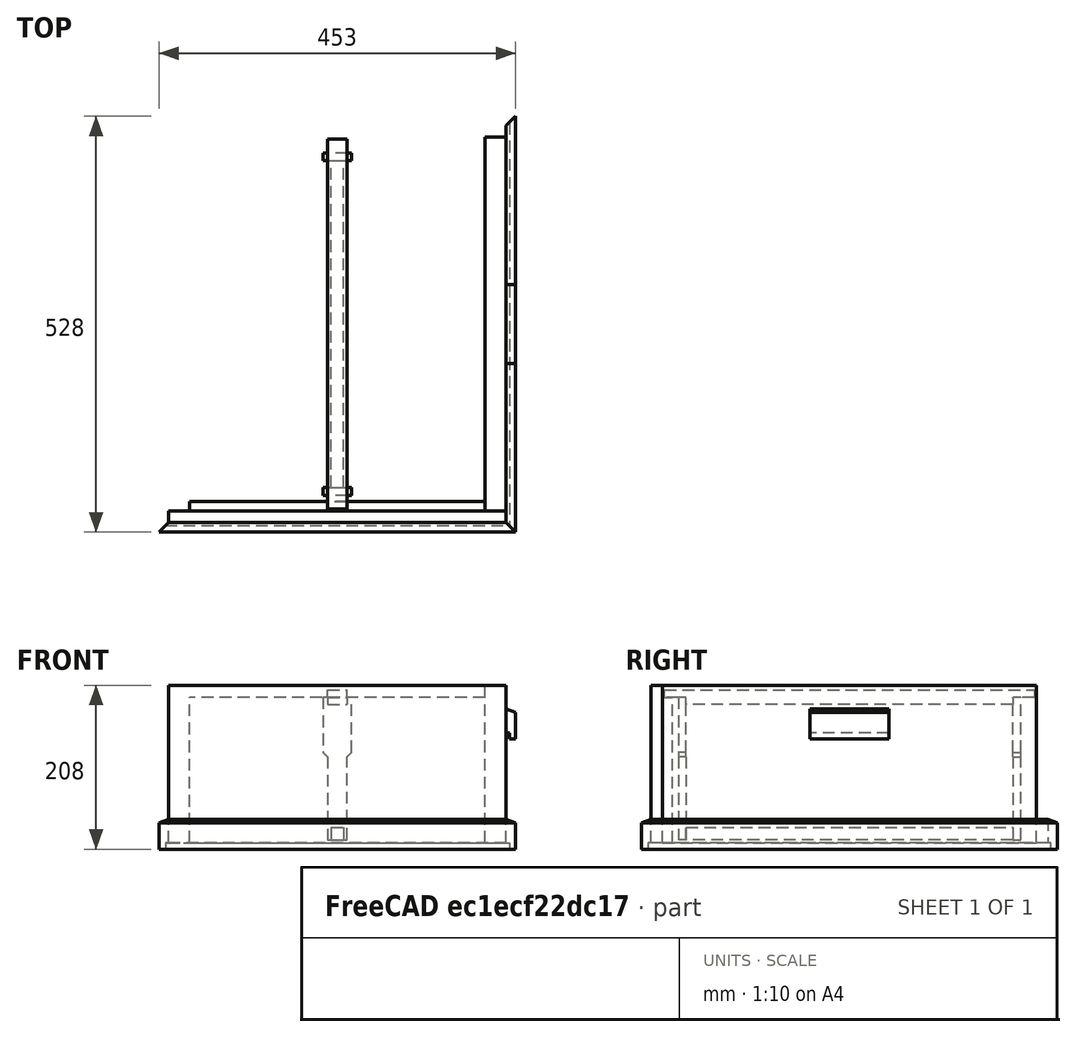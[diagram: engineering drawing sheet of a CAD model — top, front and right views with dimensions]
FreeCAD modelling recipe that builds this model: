
FCSTD DOCUMENT  (FreeCAD 0.19R)
Label: naklada_nizka
License: All rights reserved
LicenseURL: http://en.wikipedia.org/wiki/All_rights_reserved
objects: TechDraw::DrawViewDimension×33, App::Link×20, PartDesign::CoordinateSystem×16, Sketcher::SketchObject×12, TechDraw::DrawProjGroupItem×10, PartDesign::Pad×9, App::Part×7, PartDesign::Body×6, TechDraw::DrawProjGroup×5, TechDraw::DrawViewPart×4, TechDraw::DrawRichAnno×4, App::DocumentObjectGroup×3, PartDesign::Pocket×3, TechDraw::DrawSVGTemplate×3, TechDraw::DrawPage×3, TechDraw::DrawViewSection×2, TechDraw::DrawViewAnnotation×2, App::FeaturePython×1
note: 58 computed .brp shape members not serialized (recipe doc carries the construction recipe); baked Part::Feature solids carry a one-line shape summary decoded from their .brp

FEATURE [PartDesign::CoordinateSystem] LCS_Origin
  AttacherType = Attacher::AttachEngine3D
  MapMode = 2
  Support = -> [X_Axis]
FEATURE [App::FeaturePython] Variables  # WARN: FeaturePython — macro-defined, semantics opaque (R4)
  Type = App::PropertyContainer
  frame_cut = 15
  frame_height = 190
  frame_spacing = 37.5
  height = 200
  inner_depth = 450
  inner_width = 375
  wall_cut = 12.5
  wall_thickness = 27
FEATURE [App::DocumentObjectGroup] Constraints
FEATURE [App::DocumentObjectGroup] Configurations
FEATURE [PartDesign::CoordinateSystem] LCS_0
  AttacherType = Attacher::AttachEngine3D
  MapMode = 2
  Support = -> [X_Axis001]
FEATURE [PartDesign::CoordinateSystem] LCS_0001
  AttacherType = Attacher::AttachEngine3D
  MapMode = 2
  Support = -> [X_Axis002]
FEATURE [Sketcher::SketchObject] Sketch  label="Sketch001"
  FullyConstrained = true
  MapMode = 5
  Support = -> [XY_Plane002]
  expr: Constraints[16] = Variables.inner_width
  expr: Constraints[17] = Variables.wall_thickness
  expr: Constraints[22] = Variables.inner_depth / 2
  expr: Constraints[19] = Variables.wall_thickness
  expr: Constraints[18] = Variables.wall_cut
  sketch-geometry (8):
    g0: LineSegment StartX=-187.5 StartY=-225 StartZ=0 EndX=187.5 EndY=-225 EndZ=0
    g1: LineSegment StartX=187.5 StartY=-225 StartZ=0 EndX=187.5 EndY=-237.5 EndZ=0
    g2: LineSegment StartX=187.5 StartY=-237.5 StartZ=0 EndX=214.5 EndY=-237.5 EndZ=0
    g3: LineSegment StartX=214.5 StartY=-237.5 StartZ=0 EndX=214.5 EndY=-252 EndZ=0
    g4: LineSegment StartX=214.5 StartY=-252 StartZ=0 EndX=-214.5 EndY=-252 EndZ=0
    g5: LineSegment StartX=-214.5 StartY=-252 StartZ=0 EndX=-214.5 EndY=-237.5 EndZ=0
    g6: LineSegment StartX=-214.5 StartY=-237.5 StartZ=0 EndX=-187.5 EndY=-237.5 EndZ=0
    g7: LineSegment StartX=-187.5 StartY=-237.5 StartZ=0 EndX=-187.5 EndY=-225 EndZ=0
  constraints (23):
    c: Coincident(g0,g1)
    c: Coincident(g1,g2)
    c: Horizontal(g2)
    c: Coincident(g2,g3)
    c: Vertical(g3)
    c: Coincident(g3,g4)
    c: Horizontal(g4)
    c: Coincident(g4,g5)
    c: Vertical(g5)
    c: Coincident(g5,g6)
    c: Horizontal(g6)
    c: Coincident(g6,g7)
    c: Vertical(g7)
    c: Vertical(g1)
    c: Horizontal(g6,g1)
    c: Equal(g6,g2)
    c: DistanceX(g0,g0) = 375
    c: DistanceX(g2,g2) = 27
    c: DistanceY(g1,g1) = 12.5
    c: DistanceY(g3,g0) = 27
    c: Coincident(g0,g7)
    c: Symmetric(g0,g0,g-2)
    c: DistanceY(g0,g-1) = 225
FEATURE [PartDesign::Pad] Pad
  Direction = (1,1,1)
  Length = 200
  Length2 = 100
  Profile = -> Sketch
  Type = 0
  expr: Length = Variables.height
FEATURE [Sketcher::SketchObject] Sketch001  label="Sketch002"
  ExternalGeometry = -> [Pad]
  FullyConstrained = true
  MapMode = 5
  Placement = pos=(0,0,0) rot=(0.57735,0.57735,0.57735;2.0944rad)
  Support = -> [YZ_Plane002]
  expr: Constraints[9] = Variables.frame_cut
  sketch-geometry (4):
    g0: LineSegment StartX=-225 StartY=200 StartZ=0 EndX=-237.5 EndY=200 EndZ=0
    g1: LineSegment StartX=-237.5 StartY=200 StartZ=0 EndX=-237.5 EndY=185 EndZ=0
    g2: LineSegment StartX=-237.5 StartY=185 StartZ=0 EndX=-225 EndY=185 EndZ=0
    g3: LineSegment StartX=-225 StartY=185 StartZ=0 EndX=-225 EndY=200 EndZ=0
  constraints (10):
    c: Coincident(g0,g1)
    c: Coincident(g1,g2)
    c: Coincident(g2,g3)
    c: Coincident(g3,g0)
    c: Horizontal(g2)
    c: Vertical(g1)
    c: Vertical(g3)
    c: Coincident(g0,g-3)
    c: Coincident(g0,g-3)
    c: DistanceY(g3,g3) = 15
FEATURE [PartDesign::Pocket] Pocket
  BaseFeature = -> Pad
  Length = 5
  Length2 = 100
  Midplane = true
  Profile = -> Sketch001
  Type = 1
FEATURE [PartDesign::Body] Body
  Group = -> [LCS_0001,Sketch,Pad,Sketch001,Pocket]
  Origin = -> Origin002
  Tip = -> Pocket
FEATURE [App::Part] Wall_rear  label="wall_front_rear"
  Group = -> [LCS_0,Body]
  LabelDocUser = naklada
  LabelPartUser = Wall_rear
  Origin = -> Origin001
  PadLengthUser = 305.0 
  ShapeLengthUser = 890
  ShapeVolumeUser = 305.0 mm x 25.0 mm x 420.0 mm
FEATURE [App::Link] Wall_rear001  label="wall_front"
  AssemblyType = Part::Link
  AttachedBy = #LCS_0
  AttachedTo = Parent Assembly#LCS_Origin
  LinkedObject = -> Wall_rear
  SolverId = Asm4EE
  expr: Placement = LCS_Origin.Placement * AttachmentOffset * LCS_0.Placement ^ -1
FEATURE [App::Link] Wall_rear002  label="wall_rear"
  AssemblyType = Part::Link
  AttachedBy = #LCS_0
  AttachedTo = Parent Assembly#LCS_Origin
  AttachmentOffset = pos=(0,0,0) rot=(0,0,1;3.14159rad)
  LinkPlacement = pos=(0,0,0) rot=(0,0,1;3.14159rad)
  LinkedObject = -> Wall_rear
  Placement = pos=(0,0,0) rot=(0,0,1;3.14159rad)
  SolverId = Asm4EE
  expr: Placement = LCS_Origin.Placement * AttachmentOffset * LCS_0.Placement ^ -1
FEATURE [PartDesign::CoordinateSystem] LCS_0002  label="LCS_21"
  AttacherType = Attacher::AttachEngine3D
  MapMode = 2
  Support = -> [X_Axis003]
FEATURE [PartDesign::CoordinateSystem] LCS_0003
  AttacherType = Attacher::AttachEngine3D
  MapMode = 2
  Support = -> [X_Axis004]
FEATURE [Sketcher::SketchObject] Sketch002  label="Sketch003"
  FullyConstrained = true
  MapMode = 5
  Support = -> [XY_Plane004]
  expr: Constraints[6] = Variables.wall_thickness
  expr: Constraints[7] = Variables.inner_depth + Variables.wall_cut * 2
  expr: Constraints[8] = Variables.inner_width / 2
  sketch-geometry (4):
    g0: LineSegment StartX=187.5 StartY=-237.5 StartZ=0 EndX=214.5 EndY=-237.5 EndZ=0
    g1: LineSegment StartX=214.5 StartY=-237.5 StartZ=0 EndX=214.5 EndY=237.5 EndZ=0
    g2: LineSegment StartX=214.5 StartY=237.5 StartZ=0 EndX=187.5 EndY=237.5 EndZ=0
    g3: LineSegment StartX=187.5 StartY=237.5 StartZ=0 EndX=187.5 EndY=-237.5 EndZ=0
  constraints (11):
    c: Coincident(g0,g1)
    c: Coincident(g1,g2)
    c: Coincident(g2,g3)
    c: Coincident(g3,g0)
    c: Horizontal(g0)
    c: Horizontal(g2)
    c: DistanceX(g0,g0) = 27
    c: DistanceY(g1,g1) = 475
    c: DistanceX(g-1,g0) = 187.5
    c: Vertical(g1)
    c: Symmetric(g0,g2,g-1)
FEATURE [PartDesign::Pad] Pad001
  Direction = (1,1,1)
  Length = 200
  Length2 = 100
  Profile = -> Sketch002
  Type = 0
  expr: Length = Variables.height
FEATURE [PartDesign::Body] Body_2
  Group = -> [LCS_0003,Sketch002,Pad001]
  Origin = -> Origin004
  Tip = -> Pad001
FEATURE [App::Part] wall_side
  Group = -> [LCS_0002,Body_2]
  LabelDocUser = naklada
  LabelPartUser = wall_side
  Origin = -> Origin003
  PadLengthUser = 305.0 
  ShapeLengthUser = 1000
  ShapeVolumeUser = 305.0 mm x 475.0 mm x 25.0 mm
FEATURE [App::Link] wall_side001  label="wall_right"
  AssemblyType = Part::Link
  AttachedBy = #LCS_0002
  AttachedTo = Parent Assembly#LCS_Origin
  LinkedObject = -> wall_side
  SolverId = Asm4EE
  expr: Placement = LCS_Origin.Placement * AttachmentOffset * LCS_0002.Placement ^ -1
FEATURE [App::Link] wall  label="wall_left"
  AssemblyType = Part::Link
  AttachedBy = #LCS_0002
  AttachedTo = Parent Assembly#LCS_Origin
  AttachmentOffset = pos=(0,0,0) rot=(0,0,1;3.14159rad)
  LinkPlacement = pos=(0,0,0) rot=(0,0,1;3.14159rad)
  LinkedObject = -> wall_side
  Placement = pos=(0,0,0) rot=(0,0,1;3.14159rad)
  SolverId = Asm4EE
  expr: Placement = LCS_Origin.Placement * AttachmentOffset * LCS_0002.Placement ^ -1
FEATURE [PartDesign::CoordinateSystem] LCS_0004
  AttacherType = Attacher::AttachEngine3D
  MapMode = 2
  Support = -> [X_Axis005]
FEATURE [PartDesign::CoordinateSystem] LCS_0005
  AttacherType = Attacher::AttachEngine3D
  MapMode = 2
  Support = -> [X_Axis006]
FEATURE [Sketcher::SketchObject] Sketch003  label="Sketch004"
  FullyConstrained = true
  MapMode = 5
  Placement = pos=(0,0,0) rot=(1,0,0;1.5708rad)
  Support = -> [XZ_Plane006]
  expr: Constraints[12] = Variables.inner_width / 2 + Variables.wall_thickness
  sketch-geometry (6):
    g0: LineSegment StartX=214.5 StartY=0 StartZ=0 EndX=218.5 EndY=0 EndZ=0
    g1: LineSegment StartX=218.5 StartY=0 StartZ=0 EndX=218.5 EndY=-8 EndZ=0
    g2: LineSegment StartX=218.5 StartY=-8 StartZ=0 EndX=226.5 EndY=-8 EndZ=0
    g3: LineSegment StartX=226.5 StartY=-8 StartZ=0 EndX=226.5 EndY=25.6324 EndZ=0
    g4: LineSegment StartX=214.5 StartY=30 StartZ=0 EndX=214.5 EndY=0 EndZ=0
    g5: LineSegment StartX=214.5 StartY=30 StartZ=0 EndX=226.5 EndY=25.6324 EndZ=0
  constraints (18):
    c: Horizontal(g0)
    c: Coincident(g0,g1)
    c: Vertical(g1)
    c: Coincident(g1,g2)
    c: Horizontal(g2)
    c: Coincident(g2,g3)
    c: Vertical(g3)
    c: Coincident(g4,g0)
    c: Vertical(g4)
    c: DistanceX(g0,g0) = 4  'c'
    c: DistanceY(g1,g1) = 8  'd'
    c: Horizontal(g0,g-1)
    c: DistanceX(g-1,g0) = 214.5
    c: DistanceX(g0,g2) = 12  'a'
    c: DistanceY(g4,g4) = 30  'b'
    c: Coincident(g5,g4)
    c: Coincident(g5,g3)
    c: Angle(g5) = -0.349066  'e'
FEATURE [PartDesign::Pad] Pad002
  Direction = (1,1,1)
  Length = 700
  Length2 = 100
  Midplane = true
  Placement = pos=(0,0,0) rot=(1,0,0;1.5708rad)
  Profile = -> Sketch003
  Type = 0
FEATURE [Sketcher::SketchObject] Sketch004  label="Sketch005"
  ExternalGeometry = -> [Pad002]
  FullyConstrained = true
  MapMode = 5
  Support = -> [XY_Plane006]
  expr: Constraints[14] = Variables.inner_depth + 2 * Variables.wall_thickness
  sketch-geometry (8):
    g0: LineSegment StartX=226.5 StartY=-350 StartZ=0 EndX=226.5 EndY=-264 EndZ=0
    g1: LineSegment StartX=226.5 StartY=-264 StartZ=0 EndX=214.5 EndY=-252 EndZ=0
    g2: LineSegment StartX=214.5 StartY=-252 StartZ=0 EndX=214.5 EndY=-350 EndZ=0
    g3: LineSegment StartX=226.5 StartY=350 StartZ=0 EndX=226.5 EndY=264 EndZ=0
    g4: LineSegment StartX=226.5 StartY=264 StartZ=0 EndX=214.5 EndY=252 EndZ=0
    g5: LineSegment StartX=214.5 StartY=252 StartZ=0 EndX=214.5 EndY=350 EndZ=0
    g6: LineSegment StartX=214.5 StartY=-350 StartZ=0 EndX=226.5 EndY=-350 EndZ=0
    g7: LineSegment StartX=214.5 StartY=350 StartZ=0 EndX=226.5 EndY=350 EndZ=0
  constraints (20):
    c: Coincident(g0,g-4)
    c: Coincident(g1,g0)
    c: Coincident(g2,g1)
    c: Coincident(g2,g-4)
    c: Vertical(g2)
    c: Vertical(g0)
    c: Coincident(g-3,g3)
    c: Vertical(g3)
    c: Coincident(g3,g4)
    c: Coincident(g4,g5)
    c: Coincident(g5,g-3)
    c: Vertical(g5)
    c: Equal(g4,g1)
    c: Equal(g5,g2)
    c: DistanceY(g1,g4) = 504
    c: Coincident(g6,g2)
    c: Coincident(g6,g0)
    c: Coincident(g7,g5)
    c: Coincident(g7,g3)
    c: Perpendicular(g4,g1)
FEATURE [PartDesign::Pocket] Pocket001
  BaseFeature = -> Pad002
  Length = 41
  Length2 = 100
  Midplane = true
  Placement = pos=(0,0,0) rot=(1,0,0;1.5708rad)
  Profile = -> Sketch004
  Type = 1
FEATURE [PartDesign::Body] Body_3
  Group = -> [LCS_0005,Sketch003,Pad002,Sketch004,Pocket001]
  Origin = -> Origin006
  Tip = -> Pocket001
FEATURE [App::Part] Slat  label="slat_side"
  Group = -> [LCS_0004,Body_3]
  Origin = -> Origin005
FEATURE [PartDesign::CoordinateSystem] LCS_0006
  AttacherType = Attacher::AttachEngine3D
  MapMode = 2
  Support = -> [X_Axis007]
FEATURE [PartDesign::CoordinateSystem] LCS_0007
  AttacherType = Attacher::AttachEngine3D
  MapMode = 2
  Support = -> [X_Axis008]
FEATURE [Sketcher::SketchObject] Sketch005  label="Sketch006"
  FullyConstrained = true
  MapMode = 5
  Placement = pos=(0,0,0) rot=(0.57735,0.57735,0.57735;2.0944rad)
  Support = -> [YZ_Plane008]
  expr: Constraints[17] = Variables.inner_depth / 2 + Variables.wall_thickness
  sketch-geometry (6):
    g0: LineSegment StartX=-252 StartY=0 StartZ=0 EndX=-252 EndY=30 EndZ=0
    g1: LineSegment StartX=-264 StartY=25.6324 StartZ=0 EndX=-264 EndY=-8 EndZ=0
    g2: LineSegment StartX=-264 StartY=-8 StartZ=0 EndX=-256 EndY=-8 EndZ=0
    g3: LineSegment StartX=-256 StartY=-8 StartZ=0 EndX=-256 EndY=0 EndZ=0
    g4: LineSegment StartX=-256 StartY=0 StartZ=0 EndX=-252 EndY=0 EndZ=0
    g5: LineSegment StartX=-264 StartY=25.6324 StartZ=0 EndX=-252 EndY=30 EndZ=0
  constraints (18):
    c: Vertical(g0)
    c: Vertical(g1)
    c: Coincident(g1,g2)
    c: Horizontal(g2)
    c: Coincident(g2,g3)
    c: Vertical(g3)
    c: Coincident(g3,g4)
    c: Coincident(g4,g0)
    c: Horizontal(g4)
    c: Horizontal(g0,g-1)
    c: DistanceX(g4,g4) = 4
    c: DistanceY(g3,g3) = 8
    c: DistanceX(g1,g0) = 12
    c: DistanceY(g0,g0) = 30
    c: Coincident(g5,g1)
    c: Coincident(g5,g0)
    c: Angle(g5) = 0.349066
    c: DistanceX(g0,g-1) = 252
FEATURE [PartDesign::Pad] Pad003
  Direction = (1,1,1)
  Length = 700
  Length2 = 100
  Midplane = true
  Placement = pos=(0,0,0) rot=(0.57735,0.57735,0.57735;2.0944rad)
  Profile = -> Sketch005
  Type = 0
FEATURE [Sketcher::SketchObject] Sketch006  label="Sketch007"
  ExternalGeometry = -> [Pad003]
  FullyConstrained = true
  MapMode = 5
  Support = -> [XY_Plane008]
  expr: Constraints[19] = Variables.inner_width + 2 * Variables.wall_thickness
  sketch-geometry (8):
    g0: LineSegment StartX=-350 StartY=-264 StartZ=0 EndX=-350 EndY=-252 EndZ=0
    g1: LineSegment StartX=-350 StartY=-252 StartZ=0 EndX=-214.5 EndY=-252 EndZ=0
    g2: LineSegment StartX=-214.5 StartY=-252 StartZ=0 EndX=-226.5 EndY=-264 EndZ=0
    g3: LineSegment StartX=-226.5 StartY=-264 StartZ=0 EndX=-350 EndY=-264 EndZ=0
    g4: LineSegment StartX=350 StartY=-264 StartZ=0 EndX=350 EndY=-252 EndZ=0
    g5: LineSegment StartX=350 StartY=-252 StartZ=0 EndX=214.5 EndY=-252 EndZ=0
    g6: LineSegment StartX=214.5 StartY=-252 StartZ=0 EndX=226.5 EndY=-264 EndZ=0
    g7: LineSegment StartX=226.5 StartY=-264 StartZ=0 EndX=350 EndY=-264 EndZ=0
  constraints (20):
    c: Coincident(g-3,g0)
    c: Coincident(g0,g-3)
    c: Coincident(g0,g1)
    c: Coincident(g1,g2)
    c: Coincident(g2,g3)
    c: Coincident(g3,g0)
    c: Coincident(g-4,g4)
    c: Coincident(g4,g-4)
    c: Coincident(g4,g5)
    c: Coincident(g5,g6)
    c: Coincident(g6,g7)
    c: Coincident(g7,g4)
    c: Perpendicular(g2,g6)
    c: Equal(g2,g6)
    c: Equal(g1,g5)
    c: Horizontal(g1)
    c: Horizontal(g3)
    c: Horizontal(g7)
    c: Horizontal(g5)
    c: DistanceX(g1,g5) = 429
FEATURE [PartDesign::Pocket] Pocket002
  BaseFeature = -> Pad003
  Length = 5
  Length2 = 100
  Midplane = true
  Placement = pos=(0,0,0) rot=(0.57735,0.57735,0.57735;2.0944rad)
  Profile = -> Sketch006
  Type = 1
FEATURE [PartDesign::Body] Body_4
  Group = -> [LCS_0007,Sketch005,Pad003,Sketch006,Pocket002]
  Origin = -> Origin008
  Tip = -> Pocket002
FEATURE [App::Part] Slat2  label="slat_front_rear"
  Group = -> [LCS_0006,Body_4]
  Origin = -> Origin007
FEATURE [App::Link] Slat003  label="slat_right"
  AssemblyType = Part::Link
  AttachedBy = #LCS_0004
  AttachedTo = Parent Assembly#LCS_Origin
  LinkedObject = -> Slat
  SolverId = Asm4EE
  expr: Placement = LCS_Origin.Placement * AttachmentOffset * LCS_0004.Placement ^ -1
FEATURE [App::Link] Slat2001  label="slat_front"
  AssemblyType = Part::Link
  AttachedBy = #LCS_0006
  AttachedTo = Parent Assembly#LCS_Origin
  LinkedObject = -> Slat2
  SolverId = Asm4EE
  expr: Placement = LCS_Origin.Placement * AttachmentOffset * LCS_0006.Placement ^ -1
FEATURE [App::Link] Slat2002  label="slat_left"
  AssemblyType = Part::Link
  AttachedBy = #LCS_0004
  AttachedTo = Parent Assembly#LCS_Origin
  AttachmentOffset = pos=(0,0,0) rot=(0,0,1;3.14159rad)
  LinkPlacement = pos=(0,0,0) rot=(0,0,1;3.14159rad)
  LinkedObject = -> Slat
  Placement = pos=(0,0,0) rot=(0,0,1;3.14159rad)
  SolverId = Asm4EE
  expr: Placement = LCS_Origin.Placement * AttachmentOffset * LCS_0004.Placement ^ -1
FEATURE [App::Link] Slat2003  label="slat_rear"
  AssemblyType = Part::Link
  AttachedBy = #LCS_0006
  AttachedTo = Parent Assembly#LCS_Origin
  AttachmentOffset = pos=(0,0,0) rot=(0,0,1;3.14159rad)
  LinkPlacement = pos=(0,0,0) rot=(0,0,1;3.14159rad)
  LinkedObject = -> Slat2
  Placement = pos=(0,0,0) rot=(0,0,1;3.14159rad)
  SolverId = Asm4EE
  expr: Placement = LCS_Origin.Placement * AttachmentOffset * LCS_0006.Placement ^ -1
FEATURE [Sketcher::SketchObject] Sketch007  label="Sketch008"
  FullyConstrained = true
  MapMode = 5
  Placement = pos=(0,0,0) rot=(1,0,0;1.5708rad)
  Support = -> [XZ_Plane009]
  expr: Constraints[11] = Variables.inner_width / 2 + Variables.wall_thickness
  expr: Constraints[17] = Variables.height - 30
  sketch-geometry (6):
    g0: LineSegment StartX=214.5 StartY=140 StartZ=0 EndX=218.5 EndY=140 EndZ=0
    g1: LineSegment StartX=218.5 StartY=140 StartZ=0 EndX=218.5 EndY=132 EndZ=0
    g2: LineSegment StartX=218.5 StartY=132 StartZ=0 EndX=226.5 EndY=132 EndZ=0
    g3: LineSegment StartX=226.5 StartY=132 StartZ=0 EndX=226.5 EndY=165.632 EndZ=0
    g4: LineSegment StartX=214.5 StartY=170 StartZ=0 EndX=214.5 EndY=140 EndZ=0
    g5: LineSegment StartX=214.5 StartY=170 StartZ=0 EndX=226.5 EndY=165.632 EndZ=0
  constraints (18):
    c: Horizontal(g0)
    c: Coincident(g0,g1)
    c: Vertical(g1)
    c: Coincident(g1,g2)
    c: Horizontal(g2)
    c: Coincident(g2,g3)
    c: Vertical(g3)
    c: Coincident(g4,g0)
    c: Vertical(g4)
    c: DistanceX(g0,g0) = 4  'c'
    c: DistanceY(g1,g1) = 8  'd'
    c: DistanceX(g-1,g0) = 214.5
    c: DistanceX(g0,g2) = 12  'a'
    c: DistanceY(g4,g4) = 30  'b'
    c: Coincident(g5,g4)
    c: Coincident(g5,g3)
    c: Angle(g5) = -0.349066  'e'
    c: DistanceY(g-1,g4) = 170
FEATURE [PartDesign::CoordinateSystem] LCS_0008
  AttacherType = Attacher::AttachEngine3D
  MapMode = 2
  Support = -> [X_Axis010]
FEATURE [PartDesign::CoordinateSystem] LCS_0009
  AttacherType = Attacher::AttachEngine3D
  MapMode = 2
  Support = -> [X_Axis009]
FEATURE [PartDesign::Pad] Pad004
  Direction = (1,1,1)
  Length = 100
  Length2 = 100
  Midplane = true
  Placement = pos=(0,0,0) rot=(1,0,0;1.5708rad)
  Profile = -> Sketch007
  Type = 0
FEATURE [PartDesign::Body] Body_005
  Group = -> [LCS_0008,Sketch007,Pad004]
  Origin = -> Origin009
  Tip = -> Pad004
FEATURE [App::Part] Slat2004  label="handle"
  Group = -> [LCS_0009,Body_005]
  Origin = -> Origin010
FEATURE [App::Link] Handle1  label="handle_right"
  AssemblyType = Part::Link
  AttachedBy = #LCS_0009
  AttachedTo = Parent Assembly#LCS_Origin
  LinkedObject = -> Slat2004
  SolverId = Asm4EE
  expr: Placement = LCS_Origin.Placement * AttachmentOffset * LCS_0009.Placement ^ -1
FEATURE [App::Link] Handle2  label="handle_left"
  AssemblyType = Part::Link
  AttachedBy = #LCS_0009
  AttachedTo = Parent Assembly#LCS_Origin
  AttachmentOffset = pos=(0,0,0) rot=(0,0,1;3.14159rad)
  LinkPlacement = pos=(0,0,0) rot=(0,0,1;3.14159rad)
  LinkedObject = -> Slat2004
  Placement = pos=(0,0,0) rot=(0,0,1;3.14159rad)
  SolverId = Asm4EE
  expr: Placement = LCS_Origin.Placement * AttachmentOffset * LCS_0009.Placement ^ -1
FEATURE [PartDesign::CoordinateSystem] LCS_1  label="LCS_up"
  AttacherType = Attacher::AttachEngine3D
  Placement = pos=(0,0,200) rot=(0,0,1;0rad)
  expr: .Placement.Base.z = Variables.height
FEATURE [PartDesign::CoordinateSystem] LCS_0010
  AttacherType = Attacher::AttachEngine3D
  MapMode = 2
  Support = -> [X_Axis011]
FEATURE [PartDesign::CoordinateSystem] LCS_0011
  AttacherType = Attacher::AttachEngine3D
  MapMode = 2
  Support = -> [X_Axis012]
FEATURE [Sketcher::SketchObject] Sketch008  label="Sketch009"
  FullyConstrained = true
  MapMode = 5
  Placement = pos=(0,0,0) rot=(0.57735,0.57735,0.57735;2.0944rad)
  Support = -> [YZ_Plane012]
  expr: Constraints[22] = Variables.height - Variables.frame_cut
  sketch-geometry (8):
    g0: LineSegment StartX=-235 StartY=194 StartZ=0 EndX=235 EndY=194 EndZ=0
    g1: LineSegment StartX=235 StartY=194 StartZ=0 EndX=235 EndY=185 EndZ=0
    g2: LineSegment StartX=235 StartY=185 StartZ=0 EndX=207.5 EndY=185 EndZ=0
    g3: LineSegment StartX=207.5 StartY=185 StartZ=0 EndX=207.5 EndY=176 EndZ=0
    g4: LineSegment StartX=207.5 StartY=176 StartZ=0 EndX=-207.5 EndY=176 EndZ=0
    g5: LineSegment StartX=-207.5 StartY=176 StartZ=0 EndX=-207.5 EndY=185 EndZ=0
    g6: LineSegment StartX=-207.5 StartY=185 StartZ=0 EndX=-235 EndY=185 EndZ=0
    g7: LineSegment StartX=-235 StartY=185 StartZ=0 EndX=-235 EndY=194 EndZ=0
  constraints (23):
    c: Horizontal(g0)
    c: Coincident(g0,g1)
    c: Vertical(g1)
    c: Coincident(g1,g2)
    c: Horizontal(g2)
    c: Coincident(g2,g3)
    c: Vertical(g3)
    c: Coincident(g3,g4)
    c: Horizontal(g4)
    c: Coincident(g4,g5)
    c: Vertical(g5)
    c: Coincident(g5,g6)
    c: Coincident(g6,g7)
    c: Coincident(g7,g0)
    c: Horizontal(g6)
    c: Vertical(g7)
    c: Symmetric(g5,g2,g-2)
    c: Equal(g6,g2)
    c: DistanceX(g0,g0) = 470
    c: DistanceX(g5,g2) = 415
    c: DistanceY(g1,g1) = 9
    c: DistanceY(g3,g0) = 18
    c: DistanceY(g-1,g6) = 185
FEATURE [PartDesign::Pad] Pad005
  Direction = (1,1,1)
  Length = 25
  Length2 = 100
  Midplane = true
  Placement = pos=(0,0,0) rot=(0.57735,0.57735,0.57735;2.0944rad)
  Profile = -> Sketch008
  Type = 0
FEATURE [Sketcher::SketchObject] Sketch010  label="Sketch011"
  ExternalGeometry = -> [Pad005]
  FullyConstrained = true
  MapMode = 5
  Placement = pos=(-9.13e-14,-207.5,4.57e-14) rot=(-0.57735,-0.57735,0.57735;4.18879rad)
  Support = -> [Pad005]
  expr: Constraints[21] = Variables.frame_height
  sketch-geometry (8):
    g0: LineSegment StartX=-185 StartY=18 StartZ=0 EndX=-185 EndY=-18 EndZ=0
    g1: LineSegment StartX=-185 StartY=-18 StartZ=0 EndX=-115 EndY=-18 EndZ=0
    g2: LineSegment StartX=-115 StartY=-18 StartZ=0 EndX=-109.5 EndY=-12.5 EndZ=0
    g3: LineSegment StartX=-109.5 StartY=-12.5 StartZ=0 EndX=-4 EndY=-12.5 EndZ=0
    g4: LineSegment StartX=-4 StartY=-12.5 StartZ=0 EndX=-4 EndY=12.5 EndZ=0
    g5: LineSegment StartX=-4 StartY=12.5 StartZ=0 EndX=-109.5 EndY=12.5 EndZ=0
    g6: LineSegment StartX=-109.5 StartY=12.5 StartZ=0 EndX=-115 EndY=18 EndZ=0
    g7: LineSegment StartX=-115 StartY=18 StartZ=0 EndX=-185 EndY=18 EndZ=0
  constraints (22):
    c: Coincident(g0,g1)
    c: Horizontal(g1)
    c: Coincident(g1,g2)
    c: Coincident(g2,g3)
    c: Horizontal(g3)
    c: Coincident(g3,g4)
    c: Coincident(g4,g5)
    c: Horizontal(g5)
    c: Coincident(g5,g6)
    c: Coincident(g6,g7)
    c: Coincident(g7,g0)
    c: Horizontal(g7)
    c: Vertical(g5,g2)
    c: Vertical(g1,g6)
    c: Symmetric(g0,g0,g-1)
    c: Symmetric(g4,g3,g-1)
    c: Perpendicular(g6,g2)
    c: DistanceY(g4,g4) = 25
    c: DistanceY(g0,g0) = 36
    c: DistanceX(g7,g7) = 70
    c: PointOnObject(g-3,g0)
    c: DistanceX(g-3,g4) = 190
FEATURE [PartDesign::Pad] Pad006
  BaseFeature = -> Pad005
  Direction = (1,1,1)
  Length = 10
  Length2 = 100
  Placement = pos=(0,0,0) rot=(0.57735,0.57735,0.57735;2.0944rad)
  Profile = -> Sketch010
  Type = 0
FEATURE [Sketcher::SketchObject] Sketch011  label="Sketch012"
  ExternalGeometry = -> [Pad006]
  FullyConstrained = true
  MapMode = 5
  Placement = pos=(1.143e-13,207.5,-4.56e-14) rot=(0.57735,0.57735,0.57735;4.18879rad)
  Support = -> [Pad006]
  sketch-geometry (8):
    g0: LineSegment StartX=4 StartY=12.5 StartZ=0 EndX=109.5 EndY=12.5 EndZ=0
    g1: LineSegment StartX=109.5 StartY=12.5 StartZ=0 EndX=115 EndY=18 EndZ=0
    g2: LineSegment StartX=115 StartY=18 StartZ=0 EndX=185 EndY=18 EndZ=0
    g3: LineSegment StartX=185 StartY=18 StartZ=0 EndX=185 EndY=-18 EndZ=0
    g4: LineSegment StartX=185 StartY=-18 StartZ=0 EndX=115 EndY=-18 EndZ=0
    g5: LineSegment StartX=115 StartY=-18 StartZ=0 EndX=109.5 EndY=-12.5 EndZ=0
    g6: LineSegment StartX=109.5 StartY=-12.5 StartZ=0 EndX=4 EndY=-12.5 EndZ=0
    g7: LineSegment StartX=4 StartY=-12.5 StartZ=0 EndX=4 EndY=12.5 EndZ=0
  constraints (17):
    c: Coincident(g-6,g0)
    c: Coincident(g0,g-3)
    c: Coincident(g0,g1)
    c: Coincident(g1,g-3)
    c: Coincident(g1,g2)
    c: Horizontal(g2)
    c: Coincident(g2,g3)
    c: Coincident(g3,g-5)
    c: Vertical(g3)
    c: Coincident(g3,g4)
    c: Coincident(g4,g-4)
    c: Coincident(g4,g5)
    c: Coincident(g5,g-4)
    c: Coincident(g5,g6)
    c: Coincident(g6,g-6)
    c: Coincident(g6,g7)
    c: Coincident(g7,g0)
FEATURE [PartDesign::Pad] Pad007
  BaseFeature = -> Pad006
  Direction = (1,1,1)
  Length = 10
  Length2 = 100
  Placement = pos=(0,0,0) rot=(0.57735,0.57735,0.57735;2.0944rad)
  Profile = -> Sketch011
  Type = 0
FEATURE [Sketcher::SketchObject] Sketch012  label="Sketch013"
  ExternalGeometry = -> [Pad007]
  FullyConstrained = true
  MapMode = 5
  Placement = pos=(0,0,0) rot=(0.57735,0.57735,0.57735;2.0944rad)
  Support = -> [YZ_Plane012]
  sketch-geometry (4):
    g0: LineSegment StartX=-207.5 StartY=20 StartZ=0 EndX=207.5 EndY=20 EndZ=0
    g1: LineSegment StartX=207.5 StartY=20 StartZ=0 EndX=207.5 EndY=4 EndZ=0
    g2: LineSegment StartX=207.5 StartY=4 StartZ=0 EndX=-207.5 EndY=4 EndZ=0
    g3: LineSegment StartX=-207.5 StartY=4 StartZ=0 EndX=-207.5 EndY=20 EndZ=0
  constraints (10):
    c: Coincident(g0,g1)
    c: Coincident(g1,g2)
    c: Coincident(g2,g3)
    c: Coincident(g3,g0)
    c: Horizontal(g0)
    c: Vertical(g1)
    c: Vertical(g3)
    c: Coincident(g1,g-4)
    c: Coincident(g2,g-3)
    c: DistanceY(g1,g1) = 16
FEATURE [PartDesign::Pad] Pad008
  BaseFeature = -> Pad007
  Direction = (1,1,1)
  Length = 16
  Length2 = 100
  Midplane = true
  Placement = pos=(0,0,0) rot=(0.57735,0.57735,0.57735;2.0944rad)
  Profile = -> Sketch012
  Type = 0
FEATURE [PartDesign::Body] Body_5
  Group = -> [LCS_0011,Sketch008,Pad005,Sketch010,Pad006,Sketch011,Pad007,Sketch012,Pad008]
  Origin = -> Origin012
  Tip = -> Pad008
FEATURE [PartDesign::CoordinateSystem] LCS_L
  AttacherType = Attacher::AttachEngine3D
  Placement = pos=(-18.75,0,0) rot=(0,0,1;0rad)
  expr: .Placement.Base.x = -Variables.frame_spacing / 2
FEATURE [PartDesign::CoordinateSystem] LCS_R
  AttacherType = Attacher::AttachEngine3D
  Placement = pos=(18.75,0,0) rot=(0,0,1;0rad)
  expr: .Placement.Base.x = Variables.frame_spacing / 2
FEATURE [App::Part] frame
  Group = -> [LCS_0010,Body_5,LCS_L,LCS_R]
  Origin = -> Origin011
FEATURE [App::DocumentObjectGroup] Parts
  Group = -> [Wall_rear,wall_side,Slat,Slat2,Slat2004,frame]
FEATURE [App::Link] frame001  label="frame5"
  AssemblyType = Part::Link
  AttachedBy = #LCS_R
  AttachedTo = Parent Assembly#LCS_Origin
  LinkPlacement = pos=(-18.75,0,0) rot=(0,0,1;0rad)
  LinkedObject = -> frame
  Placement = pos=(-18.75,0,0) rot=(0,0,1;0rad)
  SolverId = Asm4EE
  expr: Placement = LCS_Origin.Placement * AttachmentOffset * LCS_R.Placement ^ -1
FEATURE [App::Link] frame4
  AssemblyType = Part::Link
  AttachedBy = #LCS_R
  AttachedTo = frame001#LCS_L
  LinkPlacement = pos=(-56.25,0,0) rot=(0,0,1;0rad)
  LinkedObject = -> frame
  Placement = pos=(-56.25,0,0) rot=(0,0,1;0rad)
  SolverId = Asm4EE
  expr: Placement = frame001.Placement * LCS_L.Placement * AttachmentOffset * LCS_R.Placement ^ -1
FEATURE [App::Link] frame3
  AssemblyType = Part::Link
  AttachedBy = #LCS_R
  AttachedTo = frame4#LCS_L
  LinkPlacement = pos=(-93.75,0,0) rot=(0,0,1;0rad)
  LinkedObject = -> frame
  Placement = pos=(-93.75,0,0) rot=(0,0,1;0rad)
  SolverId = Asm4EE
  expr: Placement = frame4.Placement * LCS_L.Placement * AttachmentOffset * LCS_R.Placement ^ -1
FEATURE [App::Link] frame2
  AssemblyType = Part::Link
  AttachedBy = #LCS_R
  AttachedTo = frame3#LCS_L
  LinkPlacement = pos=(-131.25,0,0) rot=(0,0,1;0rad)
  LinkedObject = -> frame
  Placement = pos=(-131.25,0,0) rot=(0,0,1;0rad)
  SolverId = Asm4EE
  expr: Placement = frame3.Placement * LCS_L.Placement * AttachmentOffset * LCS_R.Placement ^ -1
FEATURE [App::Link] fra  label="frame1"
  AssemblyType = Part::Link
  AttachedBy = #LCS_R
  AttachedTo = frame2#LCS_L
  LinkPlacement = pos=(-168.75,0,0) rot=(0,0,1;0rad)
  LinkedObject = -> frame
  Placement = pos=(-168.75,0,0) rot=(0,0,1;0rad)
  SolverId = Asm4EE
  expr: Placement = frame2.Placement * LCS_L.Placement * AttachmentOffset * LCS_R.Placement ^ -1
FEATURE [App::Link] frame_6
  AssemblyType = Part::Link
  AttachedBy = #LCS_L
  AttachedTo = frame001#LCS_R
  LinkPlacement = pos=(18.75,0,0) rot=(0,0,1;0rad)
  LinkedObject = -> frame
  Placement = pos=(18.75,0,0) rot=(0,0,1;0rad)
  SolverId = Asm4EE
  expr: Placement = frame001.Placement * LCS_R.Placement * AttachmentOffset * LCS_L.Placement ^ -1
FEATURE [App::Link] frame7
  AssemblyType = Part::Link
  AttachedBy = #LCS_L
  AttachedTo = frame_6#LCS_R
  LinkPlacement = pos=(56.25,0,0) rot=(0,0,1;0rad)
  LinkedObject = -> frame
  Placement = pos=(56.25,0,0) rot=(0,0,1;0rad)
  SolverId = Asm4EE
  expr: Placement = frame_6.Placement * LCS_R.Placement * AttachmentOffset * LCS_L.Placement ^ -1
FEATURE [App::Link] frame8
  AssemblyType = Part::Link
  AttachedBy = #LCS_L
  AttachedTo = frame7#LCS_R
  LinkPlacement = pos=(93.75,0,0) rot=(0,0,1;0rad)
  LinkedObject = -> frame
  Placement = pos=(93.75,0,0) rot=(0,0,1;0rad)
  SolverId = Asm4EE
  expr: Placement = frame7.Placement * LCS_R.Placement * AttachmentOffset * LCS_L.Placement ^ -1
FEATURE [App::Link] frame9
  AssemblyType = Part::Link
  AttachedBy = #LCS_L
  AttachedTo = frame8#LCS_R
  LinkPlacement = pos=(131.25,0,0) rot=(0,0,1;0rad)
  LinkedObject = -> frame
  Placement = pos=(131.25,0,0) rot=(0,0,1;0rad)
  SolverId = Asm4EE
  expr: Placement = frame8.Placement * LCS_R.Placement * AttachmentOffset * LCS_L.Placement ^ -1
FEATURE [App::Link] frame10
  AssemblyType = Part::Link
  AttachedBy = #LCS_L
  AttachedTo = frame9#LCS_R
  LinkPlacement = pos=(168.75,0,0) rot=(0,0,1;0rad)
  LinkedObject = -> frame
  Placement = pos=(168.75,0,0) rot=(0,0,1;0rad)
  SolverId = Asm4EE
  expr: Placement = frame9.Placement * LCS_R.Placement * AttachmentOffset * LCS_L.Placement ^ -1
FEATURE [App::Part] Assembly
  AssemblyType = Part::Link
  Group = -> [LCS_Origin,Constraints,Configurations,Wall_rear001,Wall_rear002,wall_side001,wall,Slat003,Slat2001,Slat2002,Slat2003,Handle1,Handle2,LCS_1,frame001,frame4,frame3,frame2,fra,frame_6,frame7,frame8,frame9,frame10]
  LabelDocUser = naklada
  LabelPartUser = Assembly
  Origin = -> Origin
  Type = Assembly
FEATURE [TechDraw::DrawViewPart] View003
  CoarseView = false
  Direction = (1,0,0)
  Focus = 100
  HardHidden = false
  IsoCount = 0
  IsoHidden = false
  IsoVisible = false
  LockPosition = false
  Perspective = false
  Rotation = 0
  Scale = 0.2
  ScaleType = 0
  SeamHidden = false
  SeamVisible = true
  SmoothHidden = false
  SmoothVisible = true
  Source = -> [frame]
  X = 90.8967
  XDirection = (0,1,0)
  Y = 150
FEATURE [TechDraw::DrawViewDimension] Dimension034
  Arbitrary = false
  ArbitraryTolerances = false
  EqualTolerance = true
  FormatSpec = %.6g
  FormatSpecOverTolerance = %+.6g
  FormatSpecUnderTolerance = %+.6g
  Inverted = false
  LockPosition = false
  MeasureType = 1
  OverTolerance = 0
  References2D = -> [View003]
  Rotation = 0
  Scale = 0.2
  ScaleType = 0
  TheoreticalExact = false
  Type = 1
  UnderTolerance = 0
  X = -2.20365
  Y = 60.6307
FEATURE [TechDraw::DrawViewDimension] Dimension038
  Arbitrary = false
  ArbitraryTolerances = false
  EqualTolerance = true
  FormatSpec = %.6g
  FormatSpecOverTolerance = %+.6g
  FormatSpecUnderTolerance = %+.6g
  Inverted = false
  LockPosition = false
  MeasureType = 1
  OverTolerance = 0
  References2D = -> [View003]
  Rotation = 0
  Scale = 0.2
  ScaleType = 0
  TheoreticalExact = false
  Type = 2
  UnderTolerance = 0
  X = -55.5942
  Y = 42.3219
FEATURE [TechDraw::DrawViewDimension] Dimension045
  Arbitrary = false
  ArbitraryTolerances = false
  EqualTolerance = true
  FormatSpec = %.6g
  FormatSpecOverTolerance = %+.6g
  FormatSpecUnderTolerance = %+.6g
  Inverted = false
  LockPosition = false
  MeasureType = 1
  OverTolerance = 0
  References2D = -> [View003]
  Rotation = 0
  Scale = 0.2
  ScaleType = 0
  TheoreticalExact = false
  Type = 1
  UnderTolerance = 0
  X = -1.2514
  Y = -48.1994
FEATURE [TechDraw::DrawViewDimension] Dimension039
  Arbitrary = false
  ArbitraryTolerances = false
  EqualTolerance = true
  FormatSpec = %.6g
  FormatSpecOverTolerance = %+.6g
  FormatSpecUnderTolerance = %+.6g
  Inverted = false
  LockPosition = false
  MeasureType = 1
  OverTolerance = 0
  References2D = -> [View003]
  Rotation = 0
  Scale = 0.2
  ScaleType = 0
  TheoreticalExact = false
  Type = 2
  UnderTolerance = 0
  X = -63.3161
  Y = 41.8626
FEATURE [TechDraw::DrawViewDimension] Dimension036
  Arbitrary = false
  ArbitraryTolerances = false
  EqualTolerance = true
  FormatSpec = %.6g
  FormatSpecOverTolerance = %+.6g
  FormatSpecUnderTolerance = %+.6g
  Inverted = false
  LockPosition = false
  MeasureType = 1
  OverTolerance = 0
  References2D = -> [View003]
  Rotation = 0
  Scale = 0.2
  ScaleType = 0
  TheoreticalExact = false
  Type = 2
  UnderTolerance = 0
  X = -24.3116
  Y = -41.6219
FEATURE [TechDraw::DrawViewDimension] Dimension037
  Arbitrary = false
  ArbitraryTolerances = false
  EqualTolerance = true
  FormatSpec = %.6g
  FormatSpecOverTolerance = %+.6g
  FormatSpecUnderTolerance = %+.6g
  Inverted = false
  LockPosition = false
  MeasureType = 1
  OverTolerance = 0
  References2D = -> [View003]
  Rotation = 0
  Scale = 0.2
  ScaleType = 0
  TheoreticalExact = false
  Type = 1
  UnderTolerance = 0
  X = -51.535
  Y = -6.8617
FEATURE [TechDraw::DrawViewDimension] Dimension040
  Arbitrary = false
  ArbitraryTolerances = false
  EqualTolerance = true
  FormatSpec = %.6g
  FormatSpecOverTolerance = %+.6g
  FormatSpecUnderTolerance = %+.6g
  Inverted = false
  LockPosition = false
  MeasureType = 1
  OverTolerance = 0
  References2D = -> [View003]
  Rotation = 0
  Scale = 0.2
  ScaleType = 0
  TheoreticalExact = false
  Type = 2
  UnderTolerance = 0
  X = 51.7143
  Y = 4.18693
FEATURE [TechDraw::DrawViewSection] SectionView001  label="Section A - A"
  BaseView = -> View003
  CoarseView = false
  CutSurfaceDisplay = 2
  Direction = (0,-1,0)
  FileGeomPattern = <path>
  FileHatchPattern = <path>
  Focus = 100
  FuseBeforeCut = false
  HardHidden = false
  HatchScale = 1
  IsoCount = 0
  IsoHidden = false
  IsoVisible = false
  LockPosition = false
  NameGeomPattern = Diamant
  Perspective = false
  Rotation = 0
  Scale = 0.2
  ScaleType = 0
  SeamHidden = false
  SeamVisible = true
  SectionDirection = 0
  SectionNormal = (0,-1,0)
  SectionOrigin = (0,0,144)
  SectionSymbol = A
  SmoothHidden = false
  SmoothVisible = true
  Source = -> [frame]
  X = 174.457
  XDirection = (1,0,0)
  Y = 150.441
FEATURE [TechDraw::DrawViewDimension] Dimension043
  Arbitrary = false
  ArbitraryTolerances = false
  EqualTolerance = true
  FormatSpec = %.6g
  FormatSpecOverTolerance = %+.6g
  FormatSpecUnderTolerance = %+.6g
  Inverted = false
  LockPosition = false
  MeasureType = 1
  OverTolerance = 0
  References2D = -> [SectionView001]
  Rotation = 0
  Scale = 0.2
  ScaleType = 0
  TheoreticalExact = false
  Type = 1
  UnderTolerance = 0
  X = 7.4924
  Y = -37.8182
FEATURE [TechDraw::DrawViewDimension] Dimension042
  Arbitrary = false
  ArbitraryTolerances = false
  EqualTolerance = true
  FormatSpec = %.6g
  FormatSpecOverTolerance = %+.6g
  FormatSpecUnderTolerance = %+.6g
  Inverted = false
  LockPosition = false
  MeasureType = 1
  OverTolerance = 0
  References2D = -> [SectionView001]
  Rotation = 0
  Scale = 0.2
  ScaleType = 0
  TheoreticalExact = false
  Type = 1
  UnderTolerance = 0
  X = 13.6626
  Y = 23.8459
FEATURE [TechDraw::DrawViewDimension] Dimension041
  Arbitrary = false
  ArbitraryTolerances = false
  EqualTolerance = true
  FormatSpec = %.6g
  FormatSpecOverTolerance = %+.6g
  FormatSpecUnderTolerance = %+.6g
  Inverted = false
  LockPosition = false
  MeasureType = 1
  OverTolerance = 0
  References2D = -> [SectionView001]
  Rotation = 0
  Scale = 0.2
  ScaleType = 0
  TheoreticalExact = false
  Type = 1
  UnderTolerance = 0
  X = -0.440729
  Y = 57.766
FEATURE [TechDraw::DrawViewDimension] Dimension044
  Arbitrary = false
  ArbitraryTolerances = false
  EqualTolerance = true
  FormatSpec = %.6g
  FormatSpecOverTolerance = %+.6g
  FormatSpecUnderTolerance = %+.6g
  Inverted = false
  LockPosition = false
  MeasureType = 1
  OverTolerance = 0
  References2D = -> [SectionView001]
  Rotation = 0
  Scale = 0.2
  ScaleType = 0
  TheoreticalExact = false
  Type = 2
  UnderTolerance = 0
  X = -18.9181
  Y = 20.753
FEATURE [TechDraw::DrawRichAnno] RichTextAnnotation003
  AnnoParent = -> SectionView001
  AnnoText = <!DOCTYPE HTML PUBLIC "-//W3C//DTD HTML 4.0//EN" "http://www.w3.org/TR/REC-html40/strict.dtd">\n<html><head><meta name="qrichtext" content="1" /><style type="text/css">\np, li { white-space: pre-wrap; }\n</style></head><body style=" font-family:'Ubuntu'; font-size:11pt; font-weight:400; font-style:normal;">\n<p style=" margin-top:0px; margin-bottom:0px; margin-left:0px; margin-right:0px; -qt-block-indent:0; text-indent:0px;"><span style=" font-size:10pt;">Prerez A-A</span></p></body></html>
  LockPosition = false
  MaxWidth = -1
  Rotation = 0
  Scale = 0.2
  ScaleType = 0
  ShowFrame = false
  X = 1.44838
  Y = -51.4177
FEATURE [TechDraw::DrawSVGTemplate] Template002
  EditableTexts = AVTOR=Brane Borštnik; AVTOR_2=Risal: Janez Paternoster; DATUM=6.5.2022; MATERIAL=Les, smreka; MERILO=1:5; NAZIV=Okvir; NAZIV_2=Dadant-Blatt panj; STRAN=Stran 3/3; VIR=https://github.com/<owner>/Dadant-Blatt
  Height = 297
  Orientation = 0
  Width = 210
FEATURE [TechDraw::DrawPage] Page002  label="Page3"
  KeepUpdated = true
  NextBalloonIndex = 1
  ProjectionType = 0
  Scale = 0.2
  Template = -> Template002
  Views = -> [View003,SectionView001,Dimension034,Dimension036,Dimension037,Dimension038,Dimension039,Dimension040,Dimension041,Dimension042,Dimension043,RichTextAnnotation003,Dimension044,Dimension045]
FEATURE [TechDraw::DrawProjGroupItem] ProjItem  label="Front"
  CoarseView = false
  Direction = (0,1,0)
  Focus = 100
  HardHidden = false
  IsoCount = 0
  IsoHidden = false
  IsoVisible = false
  LockPosition = true
  Perspective = false
  Rotation = 0
  RotationVector = (-1,0,0)
  Scale = 0.2
  ScaleType = 2
  SeamHidden = false
  SeamVisible = true
  SmoothHidden = false
  SmoothVisible = true
  Source = -> [Wall_rear]
  Type = 0
  X = 0
  XDirection = (-1,0,0)
  Y = 0
FEATURE [TechDraw::DrawViewDimension] Dimension011
  Arbitrary = false
  ArbitraryTolerances = false
  EqualTolerance = true
  FormatSpec = H = %.6g ali 200 ali 175
  FormatSpecOverTolerance = %+.6g
  FormatSpecUnderTolerance = %+.6g
  Inverted = false
  LockPosition = false
  MeasureType = 1
  OverTolerance = 0
  References2D = -> [ProjItem]
  Rotation = 0
  ScaleType = 0
  TheoreticalExact = false
  Type = 2
  UnderTolerance = 0
  X = -64.9634
  Y = 0
FEATURE [TechDraw::DrawViewDimension] Dimension013
  Arbitrary = false
  ArbitraryTolerances = false
  EqualTolerance = true
  FormatSpec = (%.6g)
  FormatSpecOverTolerance = %+.6g
  FormatSpecUnderTolerance = %+.6g
  Inverted = false
  LockPosition = false
  MeasureType = 1
  OverTolerance = 0
  References2D = -> [ProjItem]
  Rotation = 0
  ScaleType = 0
  TheoreticalExact = false
  Type = 1
  UnderTolerance = 0
  X = 51.7346
  Y = 44.9168
FEATURE [TechDraw::DrawViewDimension] Dimension030
  Arbitrary = false
  ArbitraryTolerances = false
  EqualTolerance = true
  FormatSpec = %.6g
  FormatSpecOverTolerance = %+.6g
  FormatSpecUnderTolerance = %+.6g
  Inverted = false
  LockPosition = false
  MeasureType = 1
  OverTolerance = 0
  References2D = -> [ProjItem]
  Rotation = 0
  ScaleType = 0
  TheoreticalExact = false
  Type = 2
  UnderTolerance = 0
  X = -55.0499
  Y = 24.5331
FEATURE [TechDraw::DrawViewDimension] Dimension009
  Arbitrary = false
  ArbitraryTolerances = false
  EqualTolerance = true
  FormatSpec = %.6g
  FormatSpecOverTolerance = %+.6g
  FormatSpecUnderTolerance = %+.6g
  Inverted = false
  LockPosition = false
  MeasureType = 1
  OverTolerance = 0
  References2D = -> [ProjItem]
  Rotation = 0
  ScaleType = 0
  TheoreticalExact = false
  Type = 1
  UnderTolerance = 0
  X = -0.502911
  Y = 52.7957
FEATURE [TechDraw::DrawViewDimension] Dimension010
  Arbitrary = false
  ArbitraryTolerances = false
  EqualTolerance = true
  FormatSpec = %.6g
  FormatSpecOverTolerance = %+.6g
  FormatSpecUnderTolerance = %+.6g
  Inverted = false
  LockPosition = false
  MeasureType = 1
  OverTolerance = 0
  References2D = -> [ProjItem]
  Rotation = 0
  ScaleType = 0
  TheoreticalExact = false
  Type = 1
  UnderTolerance = 0
  X = -0.502911
  Y = 44.9343
FEATURE [TechDraw::DrawProjGroupItem] ProjItem001  label="Left"
  CoarseView = false
  Direction = (1,1e-16,0)
  Focus = 100
  HardHidden = false
  IsoCount = 0
  IsoHidden = false
  IsoVisible = false
  LockPosition = false
  Perspective = false
  Rotation = 0
  RotationVector = (1,0,0)
  Scale = 0.2
  ScaleType = 2
  SeamHidden = false
  SeamVisible = true
  SmoothHidden = false
  SmoothVisible = true
  Source = -> [Wall_rear]
  Type = 1
  X = 75.6
  XDirection = (-1e-16,1,0)
  Y = 0
FEATURE [TechDraw::DrawViewDimension] Dimension015
  Arbitrary = false
  ArbitraryTolerances = false
  EqualTolerance = true
  FormatSpec = %.6g
  FormatSpecOverTolerance = %+.6g
  FormatSpecUnderTolerance = %+.6g
  Inverted = false
  LockPosition = false
  MeasureType = 1
  OverTolerance = 0
  References2D = -> [ProjItem001]
  Rotation = 0
  ScaleType = 0
  TheoreticalExact = false
  Type = 1
  UnderTolerance = 0
  X = 11.2317
  Y = 44.9255
FEATURE [TechDraw::DrawViewDimension] Dimension014
  Arbitrary = false
  ArbitraryTolerances = false
  EqualTolerance = true
  FormatSpec = %.6g
  FormatSpecOverTolerance = %+.6g
  FormatSpecUnderTolerance = %+.6g
  Inverted = false
  LockPosition = false
  MeasureType = 1
  OverTolerance = 0
  References2D = -> [ProjItem001]
  Rotation = 0
  ScaleType = 0
  TheoreticalExact = false
  Type = 1
  UnderTolerance = 0
  X = 10.47
  Y = 52.6456
FEATURE [TechDraw::DrawProjGroup] ProjGroup
  Anchor = -> ProjItem
  AutoDistribute = true
  LockPosition = false
  ProjectionType = 0
  Rotation = 0
  Scale = 0.2
  ScaleType = 0
  Source = -> [Wall_rear]
  Views = -> [ProjItem,ProjItem001]
  X = 94.3849
  Y = 230.952
  spacingX = 30
  spacingY = 15
FEATURE [TechDraw::DrawRichAnno] RichTextAnnotation
  AnnoParent = -> ProjItem
  AnnoText = <!DOCTYPE HTML PUBLIC "-//W3C//DTD HTML 4.0//EN" "http://www.w3.org/TR/REC-html40/strict.dtd">\n<html><head><meta name="qrichtext" content="1" /><style type="text/css">\np, li { white-space: pre-wrap; }\n</style></head><body style=" font-family:'Ubuntu'; font-size:11pt; font-weight:400; font-style:normal;">\n<p style=" margin-top:0px; margin-bottom:0px; margin-left:0px; margin-right:0px; -qt-block-indent:0; text-indent:0px;"><span style=" font-size:10pt;">Sprednja in</span></p>\n<p style=" margin-top:0px; margin-bottom:0px; margin-left:0px; margin-right:0px; -qt-block-indent:0; text-indent:0px;"><span style=" font-size:10pt;">zadnja stranica</span></p></body></html>
  LockPosition = false
  MaxWidth = -1
  Rotation = 0
  ScaleType = 0
  ShowFrame = false
  X = 0
  Y = 0
FEATURE [TechDraw::DrawProjGroupItem] ProjItem002  label="Front001"
  CoarseView = false
  Direction = (1,0,0)
  Focus = 100
  HardHidden = false
  IsoCount = 0
  IsoHidden = false
  IsoVisible = false
  LockPosition = true
  Perspective = false
  Rotation = 0
  RotationVector = (0,1,0)
  Scale = 0.2
  ScaleType = 2
  SeamHidden = false
  SeamVisible = true
  SmoothHidden = false
  SmoothVisible = true
  Source = -> [wall_side]
  Type = 0
  X = 0
  XDirection = (0,1,0)
  Y = 0
FEATURE [TechDraw::DrawViewDimension] Dimension017
  Arbitrary = false
  ArbitraryTolerances = false
  EqualTolerance = true
  FormatSpec = H = %.6g ali 200 ali 175
  FormatSpecOverTolerance = %+.6g
  FormatSpecUnderTolerance = %+.6g
  Inverted = false
  LockPosition = false
  MeasureType = 1
  OverTolerance = 0
  References2D = -> [ProjItem002]
  Rotation = 0
  ScaleType = 0
  TheoreticalExact = false
  Type = 2
  UnderTolerance = 0
  X = -57.9717
  Y = -0.317325
FEATURE [TechDraw::DrawViewDimension] Dimension016
  Arbitrary = false
  ArbitraryTolerances = false
  EqualTolerance = true
  FormatSpec = %.6g
  FormatSpecOverTolerance = %+.6g
  FormatSpecUnderTolerance = %+.6g
  Inverted = false
  LockPosition = false
  MeasureType = 1
  OverTolerance = 0
  References2D = -> [ProjItem002]
  Rotation = 0
  ScaleType = 0
  TheoreticalExact = false
  Type = 1
  UnderTolerance = 0
  X = -0.317325
  Y = 40.9717
FEATURE [TechDraw::DrawProjGroupItem] ProjItem003  label="Left001"
  CoarseView = false
  Direction = (1e-16,-1,0)
  Focus = 100
  HardHidden = false
  IsoCount = 0
  IsoHidden = false
  IsoVisible = false
  LockPosition = false
  Perspective = false
  Rotation = 0
  RotationVector = (1,0,0)
  Scale = 0.2
  ScaleType = 2
  SeamHidden = false
  SeamVisible = true
  SmoothHidden = false
  SmoothVisible = true
  Source = -> [wall_side]
  Type = 1
  X = 80.2
  XDirection = (1,1e-16,0)
  Y = 0
FEATURE [TechDraw::DrawViewDimension] Dimension018
  Arbitrary = false
  ArbitraryTolerances = false
  EqualTolerance = true
  FormatSpec = %.6g
  FormatSpecOverTolerance = %+.6g
  FormatSpecUnderTolerance = %+.6g
  Inverted = false
  LockPosition = false
  MeasureType = 1
  OverTolerance = 0
  References2D = -> [ProjItem003]
  Rotation = 0
  ScaleType = 0
  TheoreticalExact = false
  Type = 1
  UnderTolerance = 0
  X = -0.317325
  Y = 42.5584
FEATURE [TechDraw::DrawProjGroup] ProjGroup001
  Anchor = -> ProjItem002
  AutoDistribute = true
  LockPosition = false
  ProjectionType = 0
  Rotation = 0
  Scale = 0.2
  ScaleType = 0
  Source = -> [wall_side]
  Views = -> [ProjItem002,ProjItem003]
  X = 91.8443
  Y = 140.877
  spacingX = 30
  spacingY = 15
FEATURE [TechDraw::DrawRichAnno] RichTextAnnotation001
  AnnoParent = -> ProjItem002
  AnnoText = <!DOCTYPE HTML PUBLIC "-//W3C//DTD HTML 4.0//EN" "http://www.w3.org/TR/REC-html40/strict.dtd">\n<html><head><meta name="qrichtext" content="1" /><style type="text/css">\np, li { white-space: pre-wrap; }\n</style></head><body style=" font-family:'Ubuntu'; font-size:11pt; font-weight:400; font-style:normal;">\n<p style=" margin-top:0px; margin-bottom:0px; margin-left:0px; margin-right:0px; -qt-block-indent:0; text-indent:0px;"><span style=" font-size:10pt;">Leva in desna</span></p>\n<p style=" margin-top:0px; margin-bottom:0px; margin-left:0px; margin-right:0px; -qt-block-indent:0; text-indent:0px;"><span style=" font-size:10pt;">stranica</span></p></body></html>
  LockPosition = false
  MaxWidth = -1
  Rotation = 0
  ScaleType = 0
  ShowFrame = false
  X = 0
  Y = 0
FEATURE [TechDraw::DrawProjGroupItem] ProjItem004  label="Front002"
  CoarseView = false
  Direction = (0,0,1)
  Focus = 100
  HardHidden = false
  IsoCount = 0
  IsoHidden = false
  IsoVisible = false
  LockPosition = true
  Perspective = false
  Rotation = 0
  RotationVector = (1,0,0)
  Scale = 0.2
  ScaleType = 2
  SeamHidden = false
  SeamVisible = true
  SmoothHidden = false
  SmoothVisible = true
  Source = -> [Slat]
  Type = 0
  X = 0
  XDirection = (1e-16,1,0)
  Y = 0
FEATURE [TechDraw::DrawViewDimension] Dimension023
  Arbitrary = false
  ArbitraryTolerances = false
  EqualTolerance = true
  FormatSpec = %.6g
  FormatSpecOverTolerance = %+.6g
  FormatSpecUnderTolerance = %+.6g
  Inverted = false
  LockPosition = false
  MeasureType = 1
  OverTolerance = 0
  References2D = -> [ProjItem004]
  Rotation = 0
  ScaleType = 0
  TheoreticalExact = false
  Type = 1
  UnderTolerance = 0
  X = -0.440729
  Y = 11.1164
FEATURE [TechDraw::DrawProjGroupItem] ProjItem005  label="Left002"
  CoarseView = false
  Direction = (-1e-16,-1,1e-16)
  Focus = 100
  HardHidden = false
  IsoCount = 0
  IsoHidden = false
  IsoVisible = false
  LockPosition = false
  Perspective = false
  Rotation = 0
  RotationVector = (1,0,0)
  Scale = 0.2
  ScaleType = 2
  SeamHidden = false
  SeamVisible = true
  SmoothHidden = false
  SmoothVisible = true
  Source = -> [Slat]
  Type = 1
  X = 66.6
  XDirection = (0,1e-16,1)
  Y = 0
FEATURE [TechDraw::DrawProjGroup] ProjGroup002
  Anchor = -> ProjItem004
  AutoDistribute = true
  LockPosition = false
  ProjectionType = 0
  Rotation = 0
  Scale = 0.2
  ScaleType = 0
  Source = -> [Slat]
  Views = -> [ProjItem004,ProjItem005]
  X = 75.6556
  Y = 77.8761
  spacingX = 10
  spacingY = 15
FEATURE [TechDraw::DrawProjGroupItem] ProjItem006  label="Front003"
  CoarseView = false
  Direction = (0,0,1)
  Focus = 100
  HardHidden = false
  IsoCount = 0
  IsoHidden = false
  IsoVisible = false
  LockPosition = true
  Perspective = false
  Rotation = 0
  RotationVector = (1,0,0)
  Scale = 0.2
  ScaleType = 2
  SeamHidden = false
  SeamVisible = true
  SmoothHidden = false
  SmoothVisible = true
  Source = -> [Slat2]
  Type = 0
  X = 0
  XDirection = (1,0,0)
  Y = 0
FEATURE [TechDraw::DrawViewDimension] Dimension024
  Arbitrary = false
  ArbitraryTolerances = false
  EqualTolerance = true
  FormatSpec = %.6g
  FormatSpecOverTolerance = %+.6g
  FormatSpecUnderTolerance = %+.6g
  Inverted = false
  LockPosition = false
  MeasureType = 1
  OverTolerance = 0
  References2D = -> [ProjItem006]
  Rotation = 0
  ScaleType = 0
  TheoreticalExact = false
  Type = 1
  UnderTolerance = 0
  X = 0
  Y = 12.659
FEATURE [TechDraw::DrawProjGroupItem] ProjItem007  label="Left003"
  CoarseView = false
  Direction = (-1,0,1e-16)
  Focus = 100
  HardHidden = false
  IsoCount = 0
  IsoHidden = false
  IsoVisible = false
  LockPosition = false
  Perspective = false
  Rotation = 0
  RotationVector = (1,0,0)
  Scale = 0.2
  ScaleType = 2
  SeamHidden = false
  SeamVisible = true
  SmoothHidden = false
  SmoothVisible = true
  Source = -> [Slat2]
  Type = 1
  X = 59.1
  XDirection = (1e-16,0,1)
  Y = 0
FEATURE [TechDraw::DrawProjGroup] ProjGroup003
  Anchor = -> ProjItem006
  AutoDistribute = true
  LockPosition = false
  ProjectionType = 0
  Rotation = 0
  Scale = 0.2
  ScaleType = 0
  Source = -> [Slat2]
  Views = -> [ProjItem006,ProjItem007]
  X = 68.8614
  Y = 60.7437
  spacingX = 10
  spacingY = 15
FEATURE [TechDraw::DrawProjGroupItem] ProjItem008  label="Front004"
  CoarseView = false
  Direction = (0,0,1)
  Focus = 100
  HardHidden = false
  IsoCount = 0
  IsoHidden = false
  IsoVisible = false
  LockPosition = true
  Perspective = false
  Rotation = 0
  RotationVector = (1,0,0)
  Scale = 0.2
  ScaleType = 2
  SeamHidden = false
  SeamVisible = true
  SmoothHidden = false
  SmoothVisible = true
  Source = -> [Slat2004]
  Type = 0
  X = 0
  XDirection = (1e-16,1,0)
  Y = 0
FEATURE [TechDraw::DrawViewDimension] Dimension021
  Arbitrary = false
  ArbitraryTolerances = false
  EqualTolerance = true
  FormatSpec = %.6g
  FormatSpecOverTolerance = %+.6g
  FormatSpecUnderTolerance = %+.6g
  Inverted = false
  LockPosition = false
  MeasureType = 1
  OverTolerance = 0
  References2D = -> [ProjItem008]
  Rotation = 0
  ScaleType = 0
  TheoreticalExact = false
  Type = 1
  UnderTolerance = 0
  X = 0.661094
  Y = 12.0219
FEATURE [TechDraw::DrawProjGroupItem] ProjItem009  label="Left004"
  CoarseView = false
  Direction = (-1e-16,-1,1e-16)
  Focus = 100
  HardHidden = false
  IsoCount = 0
  IsoHidden = false
  IsoVisible = false
  LockPosition = false
  Perspective = false
  Rotation = 0
  RotationVector = (1,0,0)
  Scale = 0.2
  ScaleType = 2
  SeamHidden = false
  SeamVisible = true
  SmoothHidden = false
  SmoothVisible = true
  Source = -> [Slat2004]
  Type = 1
  X = 23.8
  XDirection = (0,1e-16,1)
  Y = 0
FEATURE [TechDraw::DrawProjGroup] ProjGroup004
  Anchor = -> ProjItem008
  AutoDistribute = true
  LockPosition = false
  ProjectionType = 0
  Rotation = 0
  Scale = 0.2
  ScaleType = 0
  Source = -> [Slat2004]
  Views = -> [ProjItem008,ProjItem009]
  X = 35.3841
  Y = 39.8465
  spacingX = 10
  spacingY = 15
FEATURE [TechDraw::DrawViewPart] View002
  CoarseView = false
  Direction = (0,-1,0)
  Focus = 100
  HardHidden = false
  IsoCount = 0
  IsoHidden = false
  IsoVisible = false
  LockPosition = false
  Perspective = false
  Rotation = 0
  ScaleType = 0
  SeamHidden = false
  SeamVisible = true
  SmoothHidden = false
  SmoothVisible = true
  Source = -> [Slat2004]
  X = 181.026
  XDirection = (1,0,0)
  Y = 58.2571
FEATURE [TechDraw::DrawViewDimension] Dimension028
  Arbitrary = false
  ArbitraryTolerances = false
  EqualTolerance = true
  FormatSpec = %.6g
  FormatSpecOverTolerance = %+.6g
  FormatSpecUnderTolerance = %+.6g
  Inverted = false
  LockPosition = false
  MeasureType = 1
  OverTolerance = 0
  References2D = -> [View002]
  Rotation = 0
  ScaleType = 0
  TheoreticalExact = false
  Type = 6
  UnderTolerance = 0
  X = 12.6302
  Y = 2.62915
FEATURE [TechDraw::DrawViewDimension] Dimension025
  Arbitrary = false
  ArbitraryTolerances = false
  EqualTolerance = true
  FormatSpec = %.6g
  FormatSpecOverTolerance = %+.6g
  FormatSpecUnderTolerance = %+.6g
  Inverted = false
  LockPosition = false
  MeasureType = 1
  OverTolerance = 0
  References2D = -> [View002]
  Rotation = 0
  ScaleType = 0
  TheoreticalExact = false
  Type = 2
  UnderTolerance = 0
  X = -22.9514
  Y = 0.220364
FEATURE [TechDraw::DrawViewDimension] Dimension026
  Arbitrary = false
  ArbitraryTolerances = false
  EqualTolerance = true
  FormatSpec = %.6g
  FormatSpecOverTolerance = %+.6g
  FormatSpecUnderTolerance = %+.6g
  Inverted = false
  LockPosition = false
  MeasureType = 1
  OverTolerance = 0
  References2D = -> [View002]
  Rotation = 0
  ScaleType = 0
  TheoreticalExact = false
  Type = 2
  UnderTolerance = 0
  X = -14.3404
  Y = -12.7964
FEATURE [TechDraw::DrawViewDimension] Dimension022
  Arbitrary = false
  ArbitraryTolerances = false
  EqualTolerance = true
  FormatSpec = %.6g
  FormatSpecOverTolerance = %+.6g
  FormatSpecUnderTolerance = %+.6g
  Inverted = false
  LockPosition = false
  MeasureType = 1
  OverTolerance = 0
  References2D = -> [View002]
  Rotation = 0
  ScaleType = 0
  TheoreticalExact = false
  Type = 1
  UnderTolerance = 0
  X = -0.235593
  Y = 33.2252
FEATURE [TechDraw::DrawViewDimension] Dimension027
  Arbitrary = false
  ArbitraryTolerances = false
  EqualTolerance = true
  FormatSpec = %.6g
  FormatSpecOverTolerance = %+.6g
  FormatSpecUnderTolerance = %+.6g
  Inverted = false
  LockPosition = false
  MeasureType = 1
  OverTolerance = 0
  References2D = -> [View002]
  Rotation = 0
  ScaleType = 0
  TheoreticalExact = false
  Type = 1
  UnderTolerance = 0
  X = -16.765
  Y = -22.8164
FEATURE [TechDraw::DrawViewAnnotation] Annotation
  Font = osifont
  LineSpace = 80
  LockPosition = false
  MaxWidth = -1
  Rotation = 0
  ScaleType = 0
  Text = Spodnje letvice in ro\u010daji, po 2x:
  TextSize = 5
  TextStyle = 0
  X = 57.781
  Y = 93.0138
FEATURE [TechDraw::DrawRichAnno] RichTextAnnotation002
  AnnoParent = -> View002
  AnnoText = <!DOCTYPE HTML PUBLIC "-//W3C//DTD HTML 4.0//EN" "http://www.w3.org/TR/REC-html40/strict.dtd">\n<html><head><meta name="qrichtext" content="1" /><style type="text/css">\np, li { white-space: pre-wrap; }\n</style></head><body style=" font-family:'Ubuntu'; font-size:11pt; font-weight:400; font-style:normal;">\n<p style=" margin-top:0px; margin-bottom:0px; margin-left:0px; margin-right:0px; -qt-block-indent:0; text-indent:0px;"><span style=" font-size:10pt;">M 1:1</span></p></body></html>
  LockPosition = false
  MaxWidth = -1
  Rotation = 0
  ScaleType = 0
  ShowFrame = false
  X = 0
  Y = 0
FEATURE [TechDraw::DrawSVGTemplate] Template001
  EditableTexts = AVTOR=Brane Borštnik; AVTOR_2=Risal: Janez Paternoster; DATUM=6.5.2022; MATERIAL=Les, smreka; MERILO=1:5; NAZIV=Naklada; NAZIV_2=Dadant-Blatt panj; STRAN=Stran 2/3; VIR=https://github.com/<owner>/Dadant-Blatt
  Height = 297
  Orientation = 0
  Width = 210
FEATURE [TechDraw::DrawPage] Page001  label="Page2"
  KeepUpdated = true
  NextBalloonIndex = 1
  ProjectionType = 0
  Template = -> Template001
  Views = -> [ProjGroup,Dimension009,Dimension010,Dimension011,Dimension013,Dimension014,Dimension015,RichTextAnnotation,ProjGroup001,Dimension016,Dimension017,Dimension018,RichTextAnnotation001,ProjGroup002,ProjGroup003,ProjGroup004,Dimension021,View002,Annotation,Dimension022,Dimension023,Dimension024,RichTextAnnotation002,Dimension025,Dimension026,Dimension027,Dimension028,Dimension030]
FEATURE [TechDraw::DrawViewPart] View
  CoarseView = false
  Direction = (0.577,-0.577,0.577)
  Focus = 100
  HardHidden = false
  IsoCount = 0
  IsoHidden = false
  IsoVisible = false
  LockPosition = false
  Perspective = false
  Rotation = 0
  Scale = 0.1
  ScaleType = 0
  SeamHidden = false
  SeamVisible = true
  SmoothHidden = false
  SmoothVisible = true
  Source = -> [Assembly]
  X = 68.8094
  XDirection = (0.707,0.707,0)
  Y = 80.9578
FEATURE [TechDraw::DrawViewDimension] Dimension033
  Arbitrary = false
  ArbitraryTolerances = false
  EqualTolerance = true
  FormatSpec = %.6g
  FormatSpecOverTolerance = %+.6g
  FormatSpecUnderTolerance = %+.6g
  Inverted = false
  LockPosition = false
  MeasureType = 1
  OverTolerance = 0
  References2D = -> [View]
  References3D = -> [Assembly]
  Rotation = 0
  ScaleType = 0
  TheoreticalExact = false
  Type = 0
  UnderTolerance = 0
  X = 43.828
  Y = 30.2017
FEATURE [TechDraw::DrawViewPart] View001
  CoarseView = false
  Direction = (0,0,1)
  Focus = 100
  HardHidden = false
  IsoCount = 0
  IsoHidden = false
  IsoVisible = false
  LockPosition = false
  Perspective = false
  Rotation = 0
  Scale = 0.2
  ScaleType = 0
  SeamHidden = false
  SeamVisible = true
  SmoothHidden = false
  SmoothVisible = true
  Source = -> [Assembly]
  X = 75
  XDirection = (1,0,0)
  Y = 210
FEATURE [TechDraw::DrawViewDimension] Dimension
  Arbitrary = false
  ArbitraryTolerances = false
  EqualTolerance = true
  FormatSpec = %.6g
  FormatSpecOverTolerance = %+.6g
  FormatSpecUnderTolerance = %+.6g
  Inverted = false
  LockPosition = false
  MeasureType = 1
  OverTolerance = 0
  References2D = -> [View001]
  Rotation = 0
  ScaleType = 0
  TheoreticalExact = false
  Type = 1
  UnderTolerance = 0
  X = 1.44839
  Y = 78.7851
FEATURE [TechDraw::DrawViewDimension] Dimension031
  Arbitrary = false
  ArbitraryTolerances = false
  EqualTolerance = true
  FormatSpec = %.6g
  FormatSpecOverTolerance = %+.6g
  FormatSpecUnderTolerance = %+.6g
  Inverted = false
  LockPosition = false
  MeasureType = 1
  OverTolerance = 0
  References2D = -> [View001]
  Rotation = 0
  ScaleType = 0
  TheoreticalExact = false
  Type = 2
  UnderTolerance = 0
  X = 52.5519
  Y = 2.38728
FEATURE [TechDraw::DrawViewSection] SectionView  label="Section A"
  BaseView = -> View001
  CoarseView = false
  CutSurfaceDisplay = 2
  Direction = (-1,0,0)
  FileGeomPattern = <path>
  FileHatchPattern = <path>
  Focus = 100
  FuseBeforeCut = false
  HardHidden = false
  HatchScale = 1
  IsoCount = 0
  IsoHidden = false
  IsoVisible = false
  LockPosition = false
  NameGeomPattern = Diamond
  Perspective = false
  Rotation = 0
  Scale = 0.2
  ScaleType = 0
  SeamHidden = false
  SeamVisible = true
  SectionDirection = 0
  SectionNormal = (-1,0,0)
  SectionOrigin = (0,225,148.5)
  SectionSymbol = A
  SmoothHidden = false
  SmoothVisible = true
  Source = -> [Assembly]
  X = 170
  XDirection = (0,0,1)
  Y = 210
FEATURE [TechDraw::DrawViewDimension] Dimension032
  Arbitrary = false
  ArbitraryTolerances = false
  EqualTolerance = true
  FormatSpec = %.6g
  FormatSpecOverTolerance = %+.6g
  FormatSpecUnderTolerance = %+.6g
  Inverted = false
  LockPosition = false
  MeasureType = 1
  OverTolerance = 0
  References2D = -> [SectionView]
  Rotation = 0
  ScaleType = 0
  TheoreticalExact = false
  Type = 1
  UnderTolerance = 0
  X = 1.02479
  Y = -59.6162
FEATURE [TechDraw::DrawViewAnnotation] Annotation001
  Font = osifont
  LineSpace = 80
  LockPosition = false
  MaxWidth = -1
  Rotation = 0
  ScaleType = 0
  Text = Plodi\u0161\u010dna naklada: |  - vi\u0161ina naklade = 300 mm |  - vi\u0161ina okvirja = 300 mm | Medi\u0161\u010dna naklada - optimizirana: |  - vi\u0161ina naklade = 200 mm |  - vi\u0161ina okvirja = 190 mm | Medi\u0161\u010dna naklada - standardna: |  - vi\u0161ina naklade = 175 mm |  - vi\u0161ina okvirja = 165 mm
  TextSize = 5
  TextStyle = 0
  X = 166.698
  Y = 85.5258
FEATURE [TechDraw::DrawSVGTemplate] Template
  EditableTexts = AVTOR=Brane Borštnik; AVTOR_2=Risal: Janez Paternoster; DATUM=6.5.2022; MATERIAL=Les, smreka; MERILO=1:5; NAZIV=Naklada; NAZIV_2=Dadant-Blatt panj; STRAN=Stran 1/3; VIR=https://github.com/<owner>/Dadant-Blatt
  Height = 297
  Orientation = 0
  Width = 210
FEATURE [TechDraw::DrawPage] Page  label="Page1"
  KeepUpdated = true
  NextBalloonIndex = 1
  ProjectionType = 0
  Template = -> Template
  Views = -> [View,View001,SectionView,Annotation001,Dimension,Dimension031,Dimension032,Dimension033]
note: 4 file-system paths scrubbed to <path> (originals preserved in the JSON sidecar)
